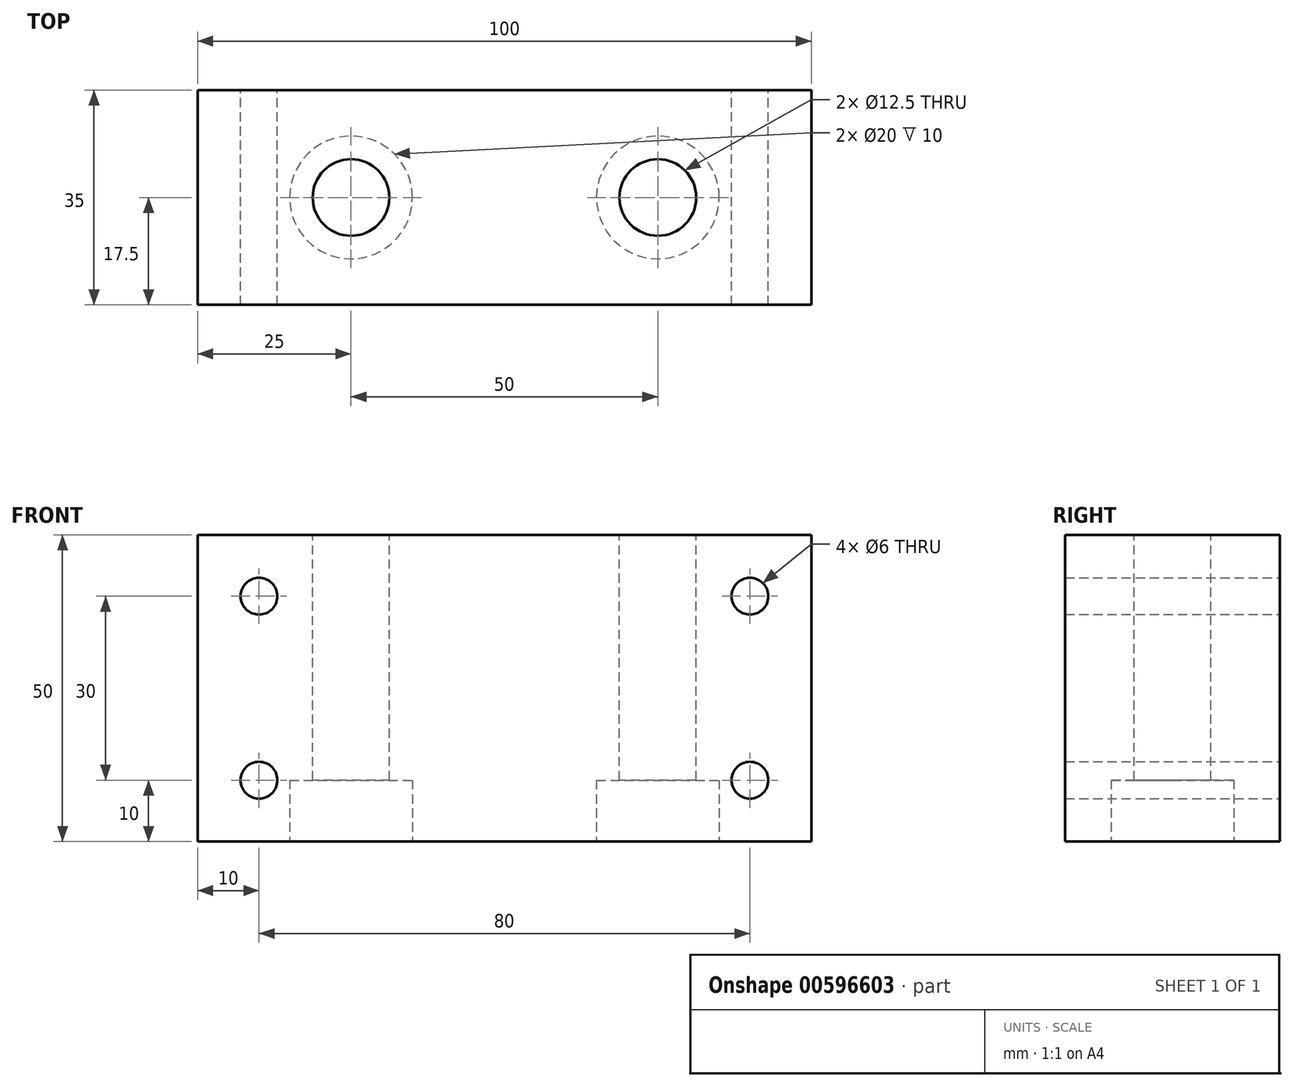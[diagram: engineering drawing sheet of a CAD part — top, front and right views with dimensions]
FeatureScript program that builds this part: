
annotation { "Feature Type Name" : "Feature", "Feature Type Description" : "" }
export const myFeature = defineFeature(function(context is Context, id is Id, definition is map)
    precondition{}
    {
        {
            var Q0;
            Q0=qCreatedBy(makeId("Front.planeOp"),FACE);
            var sketch = newSketch(context, id + "F0", { "sketchPlane" : qUnion([Q0])});
            skLineSegment(sketch, "E0.bottom", {"start": v(0, 0) * mm, "end": v(100, 0) * mm});
            skLineSegment(sketch, "E0.top", {"start": v(0, 50) * mm, "end": v(100, 50) * mm});
            skLineSegment(sketch, "E0.left", {"start": v(0, 0) * mm, "end": v(0, 50) * mm});
            skLineSegment(sketch, "E0.right", {"start": v(100, 0) * mm, "end": v(100, 50) * mm});
            skSolve(sketch);
        }
        {
            var Q0;
            Q0 = qSketchRegion(id + "F0", true);
            extrude(context, id + "F1", {"entities" : qUnion([Q0]), "depth" : 35 * mm, "offsetDistance" : 25 * mm});
        }
        {
            var Q0;
            Q0=makeQuery(id+"F1.opExtrude","SWEPT_FACE",FACE,{"disambiguationData":[OSD([sQuery(id+"F0.wireOp",EDGE,"E0.top")])]});
            var sketch = newSketch(context, id + "F2", { "sketchPlane" : qUnion([Q0])});
            skCircle(sketch, "E1", {"center": v(25, -17.5) * mm, "radius": 6.25 * mm});
            skCircle(sketch, "E2", {"center": v(75, -17.5) * mm, "radius": 6.25 * mm});
            skSolve(sketch);
        }
        {
            var Q0;
            Q0=makeQuery(id+"F2.imprint","IMPRINT",FACE,{"disambiguationData":[TD([[makeQuery(id+"F2.imprint","IMPRINT",EDGE,{"derivedFrom":sQuery(id+"F2.wireOp",EDGE,"E1")}),1.0]])]});
            var Q1;
            Q1=makeQuery(id+"F2.imprint","IMPRINT",FACE,{"disambiguationData":[TD([[makeQuery(id+"F2.imprint","IMPRINT",EDGE,{"derivedFrom":sQuery(id+"F2.wireOp",EDGE,"E2")}),1.0]])]});
            extrude(context, id + "F3", {"entities" : qUnion([Q0, Q1]), "operationType" : NewBodyOperationType.REMOVE, "endBound" : BoundingType.THROUGH_ALL, "oppositeDirection" : true, "depth" : 25 * mm, "offsetDistance" : 25 * mm});
        }
        {
            var Q0;
            Q0=makeQuery(id+"F1.opExtrude","CAP_FACE",FACE,{"disambiguationData":[OSD([sQuery(id+"F0.wireOp",EDGE,"E0.bottom"),sQuery(id+"F0.wireOp",EDGE,"E0.top"),sQuery(id+"F0.wireOp",EDGE,"E0.left"),sQuery(id+"F0.wireOp",EDGE,"E0.right")])],"isStart":true});
            var sketch = newSketch(context, id + "F4", { "sketchPlane" : qUnion([Q0])});
            skPoint(sketch, "E3", {"position": v(-90, 40) * mm});
            skPoint(sketch, "E4", {"position": v(-10, 40) * mm});
            skPoint(sketch, "E5", {"position": v(-10, 10) * mm});
            skPoint(sketch, "E6", {"position": v(-90, 10) * mm});
            skSolve(sketch);
        }
        {
            var Q0;
            Q0=sQuery(id+"F4.wireOp",VERTEX,"E3");
            var Q1;
            Q1=sQuery(id+"F4.wireOp",VERTEX,"E4");
            var Q2;
            Q2=sQuery(id+"F4.wireOp",VERTEX,"E5");
            var Q3;
            Q3=sQuery(id+"F4.wireOp",VERTEX,"E6");
            var Q4;
            Q4=makeQuery(id+"F1.opExtrude","SWEPT_BODY",BODY,{"disambiguationData":[OSD([sQuery(id+"F0.wireOp",EDGE,"E0.bottom"),sQuery(id+"F0.wireOp",EDGE,"E0.top"),sQuery(id+"F0.wireOp",EDGE,"E0.left"),sQuery(id+"F0.wireOp",EDGE,"E0.right")])]});
            hole(context, id + "F5", {"style" : HoleStyle.SIMPLE, "endStyle" : HoleEndStyle.THROUGH, "holeDiameter" : 6 * mm, "majorDiameter" : 5 * mm, "isTappedThrough" : true, "tappedDepth" : 12 * mm, "tapClearance" : 3, "startFromSketch" : true, "locations" : qUnion([Q0, Q1, Q2, Q3]), "scope" : qUnion([Q4])});
        }
        {
            var Q0;
            Q0=makeQuery(id+"F1.opExtrude","SWEPT_FACE",FACE,{"disambiguationData":[OSD([sQuery(id+"F0.wireOp",EDGE,"E0.bottom")])]});
            var sketch = newSketch(context, id + "F6", { "sketchPlane" : qUnion([Q0])});
            skCircle(sketch, "E7", {"center": v(25, 17.5) * mm, "radius": 10 * mm});
            skCircle(sketch, "E8", {"center": v(75, 17.5) * mm, "radius": 10 * mm});
            skSolve(sketch);
        }
        {
            var Q0;
            Q0=makeQuery(id+"F6.imprint","IMPRINT",FACE,{"disambiguationData":[TD([[makeQuery(id+"F6.imprint","IMPRINT",EDGE,{"derivedFrom":sQuery(id+"F6.wireOp",EDGE,"E7")}),1.0]])]});
            var Q1;
            Q1=makeQuery(id+"F6.imprint","IMPRINT",FACE,{"disambiguationData":[TD([[makeQuery(id+"F6.imprint","IMPRINT",EDGE,{"derivedFrom":sQuery(id+"F6.wireOp",EDGE,"E8")}),1.0]])]});
            extrude(context, id + "F7", {"entities" : qUnion([Q0, Q1]), "operationType" : NewBodyOperationType.REMOVE, "oppositeDirection" : true, "depth" : 10 * mm, "offsetDistance" : 25 * mm});
        }
    });
